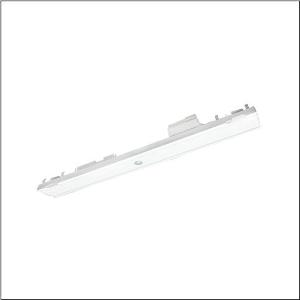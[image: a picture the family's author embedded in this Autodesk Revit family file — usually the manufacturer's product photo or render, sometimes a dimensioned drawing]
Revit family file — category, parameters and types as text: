
# Revit family: licross_r_56tl197c4x31_8620
name_source: partatom
category: Lighting Fixtures
units: mm (PartAtom-declared; Revit-internal decimal feet)

## family parameters
Cut with Voids When Loaded = No
Host = Face
Light Source = No
Part Type = Normal
Room Calculation Point = No
Round Connector Dimension = Use Diameter
Shared = No

## types (1)
- Licross® (1 x LED, 300 lm, 3.9 W, 4000K)
    Apparent Load = 4 VA
    CIE Flux Codes = 25 51 93 100 100
    Color Rendering = 70
    Color Temperature = 4000K
    Default Elevation = 1800 mm
    Description = Licross®, luminaire insert, of sheet steel, coil coated, white, length: 500mm, width: 59mm, height: 60mm, mounting height: 2.5..7m, emergency light element,LED rated luminous flux: 300lm, light colour: 740, control gear: CEAG, with plug, 6-pole, with phase selection, mains connection: 220..240V, AC/DC, 0/50..60Hz, rated input power: 3.9W, halogen-free wiring, for trunking rail, 9..14-pole, for emergency light function, supply monitoring module CEAG, with address switch, choice between two emergency light lines via tool-free moving of contact pin prior to installation in trunking rail, primary light control with lens, of PMMA, primary optical cover: cover, of PMMA, light emission: direct distribution, primary light characteristic: asymmetric,  for escape and rescue routes, compatible with all CEAG STAR technology systems (ZB-S, DG-S (DualGuard-S), LP-STAR, AT-S+), protection rating (complete): IP40, insulation class (complete): insulation class I (protective earthing), certification: CE, UKCA, protection symbol: D if used in an environment without relevant dust loads, impact resistance: IK06, permissible ambient temperature for indoor applications: -20..+40°C, packaging unit: 1 piece
    Height = 60 mm  [stored 0.19685 ft]
    Lamp = 1 x LED
    Lamp Light Flux = 300 lm
    Lamp Power = 3.9 W
    Lamp count = 1
    Length = 500 mm
    Luminous efficacy = 77 lm/W
    Manufacturer = Siteco
    ModVariant = No
    Model = 56TL197C4X31
    Mounting Place = Ceiling
    Mounting Type = Pendant
    Number of Poles = 1
    OnlyDefault = Yes
    Power Factor = 1
    Product Name = Licross®
    Product group = luminaire insert
    ProductGroupID = 901
    Protection Class = Protection class I
    Protection Degree = IP 40
    RLX_Detail_Level = 1
    RLX_Emergency_Light_Flux = 0 lm
    RLX_Emergency_Type = 0
    RLX_Emergency_Type_DB = No
    RlxData = <blob elided: 29017 chars, md5=3e1f9154>
    Socket = socket
    Standby Power = 0 W
    System Light Flux = 300 lm
    System Power = 4 W
    Type Comments = Product without accessories
    Type Image = l_1251804.jpg
    URL = http://relux.com
    VarID = ---
    Voltage = 0 V
    Weight = 0.00 kg
    Width = 59 mm

note: [stored X ft] marks values corroborated as IEEE doubles in the binary element streams (Revit-internal decimal feet)

## geometry (parser evidence)
native form markers: Blend x4, Sweep x11
no freeform markers — native parametric forms only
